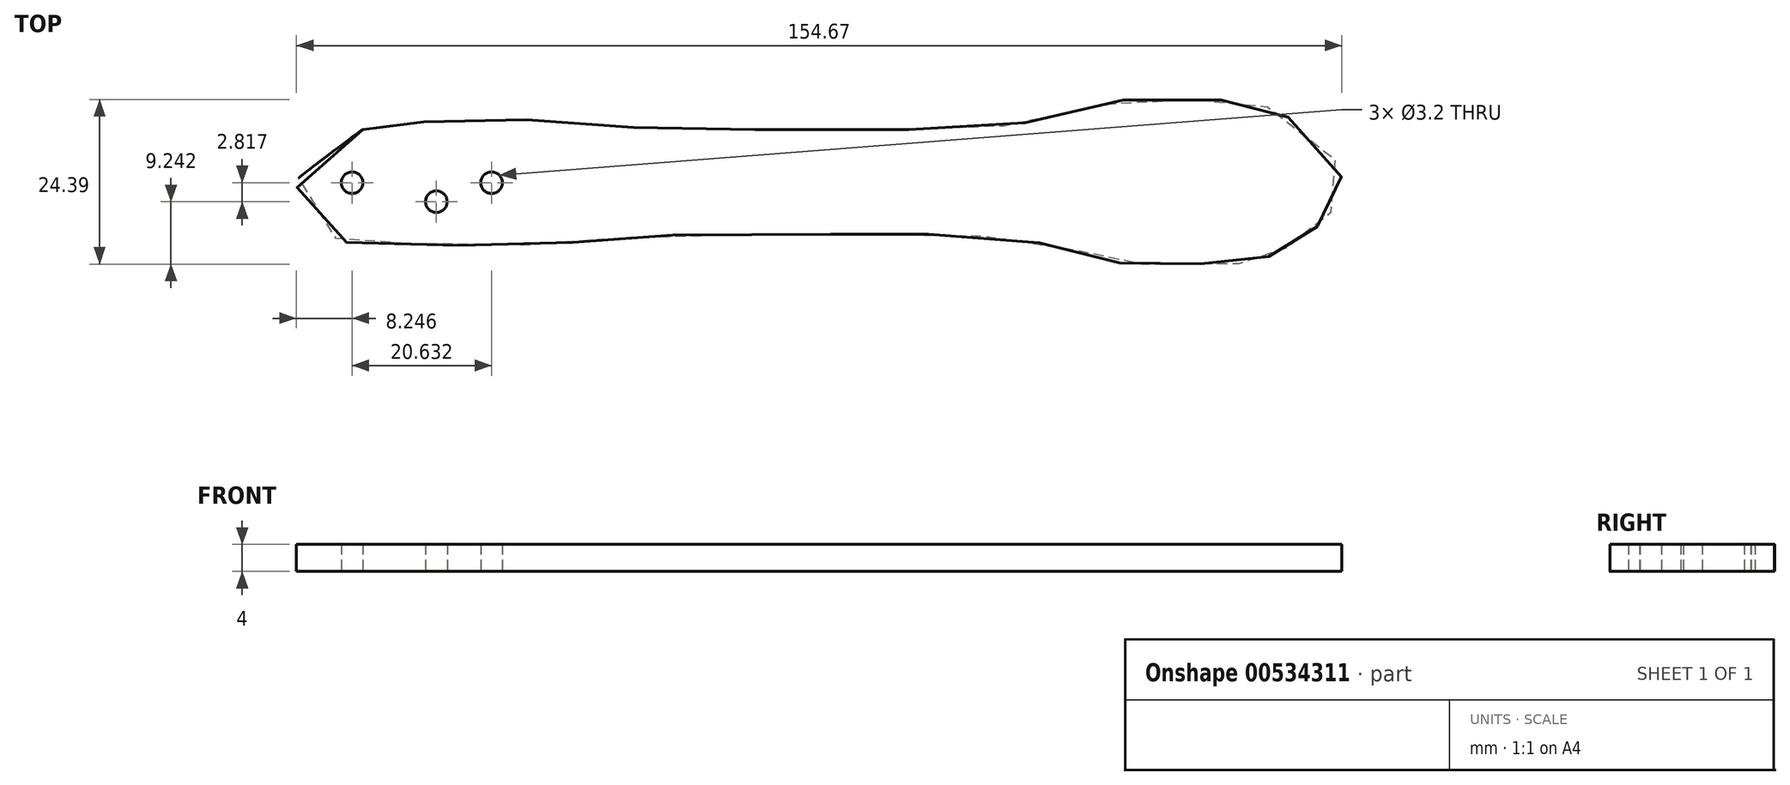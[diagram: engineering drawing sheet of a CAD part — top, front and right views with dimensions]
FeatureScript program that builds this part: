
annotation { "Feature Type Name" : "Feature", "Feature Type Description" : "" }
export const myFeature = defineFeature(function(context is Context, id is Id, definition is map)
    precondition{}
    {
        {
            var Q0;
            Q0=qCreatedBy(makeId("Top.planeOp"),FACE);
            var sketch = newSketch(context, id + "F0", { "sketchPlane" : qUnion([Q0])});
            skLineSegment(sketch, "E0", {"start": v(54.8, -3.9) * mm, "end": v(54.8, 13.58) * mm, "construction": true});
            skLineSegment(sketch, "E1", {"start": v(66.36, -3.84) * mm, "end": v(66.36, 12.93) * mm, "construction": true});
            skLineSegment(sketch, "E2", {"start": v(-48.72, -1.72) * mm, "end": v(-48.72, 12.6) * mm, "construction": true});
            skLineSegment(sketch, "E3", {"start": v(-69.35, -1.5) * mm, "end": v(-69.35, 12.87) * mm, "construction": true});
            skLineSegment(sketch, "E4", {"start": v(-69.35, 0) * mm, "end": v(-48.72, 0) * mm, "construction": true});
            skLineSegment(sketch, "E5", {"start": v(-48.72, 0) * mm, "end": v(-56.51, -2.9) * mm, "construction": true});
            skLineSegment(sketch, "E6", {"start": v(-69.35, 0) * mm, "end": v(-56.88, -2.82) * mm, "construction": true});
            skSolve(sketch);
        }
        {
            var Q0;
            Q0=qCreatedBy(makeId("Top.planeOp"),FACE);
            var sketch = newSketch(context, id + "F1", { "sketchPlane" : qUnion([Q0])});
            skPoint(sketch, "E7", {"position": v(-66.56, 8.68) * mm});
            skPoint(sketch, "E8", {"position": v(-65.15, 8.8) * mm});
            skPoint(sketch, "E9", {"position": v(-60.16, 8.9) * mm});
            skPoint(sketch, "E10", {"position": v(-54.89, 9.2) * mm});
            skPoint(sketch, "E11", {"position": v(-47.44, 9.4) * mm});
            skPoint(sketch, "E12", {"position": v(-38.58, 9.1) * mm});
            skPoint(sketch, "E13", {"position": v(-31.38, 8.43) * mm});
            skPoint(sketch, "E14", {"position": v(-23.01, 7.94) * mm});
            skPoint(sketch, "E15", {"position": v(-12.89, 7.85) * mm});
            skPoint(sketch, "E16", {"position": v(-0.18, 7.85) * mm});
            skPoint(sketch, "E17", {"position": v(16.83, 7.9) * mm});
            skPoint(sketch, "E18", {"position": v(24.53, 8.2) * mm});
            skPoint(sketch, "E19", {"position": v(34.2, 9.5) * mm});
            skPoint(sketch, "E20", {"position": v(42.25, 11.45) * mm});
            skPoint(sketch, "E21", {"position": v(44.84, 12.23) * mm});
            skPoint(sketch, "E22", {"position": v(46.52, 12.33) * mm});
            skPoint(sketch, "E23", {"position": v(54.4, 12.32) * mm});
            skPoint(sketch, "E24", {"position": v(61.48, 12.27) * mm});
            skPoint(sketch, "E25", {"position": v(62.46, 12.27) * mm});
            skPoint(sketch, "E26", {"position": v(65.35, 11.53) * mm});
            skPoint(sketch, "E27", {"position": v(69.92, 9.23) * mm});
            skPoint(sketch, "E28", {"position": v(74.4, 5.78) * mm});
            skPoint(sketch, "E29", {"position": v(76.76, 1.96) * mm});
            skPoint(sketch, "E30", {"position": v(77.07, 0.23) * mm});
            skPoint(sketch, "E31", {"position": v(76.79, -1.82) * mm});
            skPoint(sketch, "E32", {"position": v(75.79, -4) * mm});
            skPoint(sketch, "E33", {"position": v(74.1, -5.85) * mm});
            skPoint(sketch, "E34", {"position": v(72.54, -7.25) * mm});
            skPoint(sketch, "E35", {"position": v(70.5, -8.71) * mm});
            skPoint(sketch, "E36", {"position": v(68.73, -9.75) * mm});
            skPoint(sketch, "E37", {"position": v(66.81, -10.73) * mm});
            skPoint(sketch, "E38", {"position": v(64.96, -11.46) * mm});
            skPoint(sketch, "E39", {"position": v(63.48, -11.9) * mm});
            skPoint(sketch, "E40", {"position": v(61.72, -12.03) * mm});
            skPoint(sketch, "E41", {"position": v(54.35, -12.04) * mm});
            skPoint(sketch, "E42", {"position": v(47.82, -12.05) * mm});
            skPoint(sketch, "E43", {"position": v(45.56, -12.04) * mm});
            skPoint(sketch, "E44", {"position": v(43.9, -11.81) * mm});
            skPoint(sketch, "E45", {"position": v(39.53, -10.52) * mm});
            skPoint(sketch, "E46", {"position": v(34.82, -9.35) * mm});
            skPoint(sketch, "E47", {"position": v(29.16, -8.47) * mm});
            skPoint(sketch, "E48", {"position": v(20.8, -7.77) * mm});
            skPoint(sketch, "E49", {"position": v(10.86, -7.65) * mm});
            skPoint(sketch, "E50", {"position": v(3.89, -7.66) * mm});
            skPoint(sketch, "E51", {"position": v(0.57, -7.64) * mm});
            skPoint(sketch, "E52", {"position": v(-18.65, -7.72) * mm});
            skPoint(sketch, "E53", {"position": v(-27.09, -8.04) * mm});
            skPoint(sketch, "E54", {"position": v(-34.19, -8.64) * mm});
            skPoint(sketch, "E55", {"position": v(-40, -9.07) * mm});
            skPoint(sketch, "E56", {"position": v(-50.02, -9.35) * mm});
            skPoint(sketch, "E57", {"position": v(-58.85, -9.11) * mm});
            skPoint(sketch, "E58", {"position": v(-68.96, -8.92) * mm});
            skPoint(sketch, "E59", {"position": v(-70.76, -8.74) * mm});
            skPoint(sketch, "E60", {"position": v(-71.37, -8.52) * mm});
            skPoint(sketch, "E61", {"position": v(-71.8, -8.17) * mm});
            skPoint(sketch, "E62", {"position": v(-77.08, -1.38) * mm});
            skPoint(sketch, "E63", {"position": v(-77.58, -0.45) * mm});
            skPoint(sketch, "E64", {"position": v(-77.56, 0.25) * mm});
            skPoint(sketch, "E65", {"position": v(-67.4, 8.15) * mm});
            skPoint(sketch, "E66", {"position": v(-67.78, 7.88) * mm});
            skPoint(sketch, "E67", {"position": v(-76.67, 1.2) * mm});
            skFitSpline(sketch, "E68", {"points": [v(-67.78, 7.88) * mm, v(-67.4, 8.15) * mm, v(-66.56, 8.68) * mm, v(-65.15, 8.8) * mm, v(-60.16, 8.9) * mm, v(-54.89, 9.2) * mm, v(-47.44, 9.4) * mm, v(-38.58, 9.1) * mm, v(-31.38, 8.43) * mm, v(-23.01, 7.94) * mm, v(-12.89, 7.85) * mm, v(-0.18, 7.85) * mm, v(16.83, 7.9) * mm, v(24.53, 8.2) * mm, v(34.2, 9.5) * mm, v(42.25, 11.45) * mm, v(44.84, 12.23) * mm, v(46.52, 12.33) * mm, v(54.4, 12.32) * mm, v(61.48, 12.27) * mm, v(62.46, 12.27) * mm, v(65.35, 11.53) * mm, v(69.92, 9.23) * mm, v(74.4, 5.78) * mm, v(76.76, 1.96) * mm, v(77.07, 0.23) * mm, v(76.79, -1.82) * mm, v(75.79, -4) * mm, v(74.1, -5.85) * mm, v(72.54, -7.25) * mm, v(70.5, -8.71) * mm, v(68.73, -9.75) * mm, v(66.81, -10.73) * mm, v(64.96, -11.46) * mm, v(63.48, -11.9) * mm, v(61.72, -12.03) * mm, v(54.35, -12.04) * mm, v(47.82, -12.05) * mm, v(45.56, -12.04) * mm, v(43.9, -11.81) * mm, v(39.53, -10.52) * mm, v(34.82, -9.35) * mm, v(29.16, -8.47) * mm, v(20.8, -7.77) * mm, v(10.86, -7.65) * mm, v(3.89, -7.66) * mm, v(0.57, -7.64) * mm, v(-18.65, -7.72) * mm, v(-27.09, -8.04) * mm, v(-34.19, -8.64) * mm, v(-40, -9.07) * mm, v(-50.02, -9.35) * mm, v(-58.85, -9.11) * mm, v(-68.96, -8.92) * mm, v(-70.76, -8.74) * mm, v(-71.37, -8.52) * mm, v(-71.8, -8.17) * mm, v(-77.08, -1.38) * mm, v(-77.58, -0.45) * mm, v(-77.56, 0.25) * mm, v(-76.67, 1.2) * mm, v(-67.78, 7.88) * mm]});
            skPoint(sketch, "E69.0", {"position": v(-69.35, 0) * mm});
            skPoint(sketch, "E70.0", {"position": v(-48.72, 0) * mm});
            skCircle(sketch, "E71", {"center": v(-69.35, 0) * mm, "radius": 1.6 * mm});
            skCircle(sketch, "E72", {"center": v(-48.72, 0) * mm, "radius": 1.6 * mm});
            skPoint(sketch, "E73.0", {"position": v(-56.88, -2.82) * mm});
            skCircle(sketch, "E74", {"center": v(-56.88, -2.82) * mm, "radius": 1.6 * mm});
            skSolve(sketch);
        }
        {
            var Q0;
            Q0=qSketchRegion(id+"F1",true);
            extrude(context, id + "F2", {"entities" : qUnion([Q0]), "depth" : 4 * mm});
        }
    });
